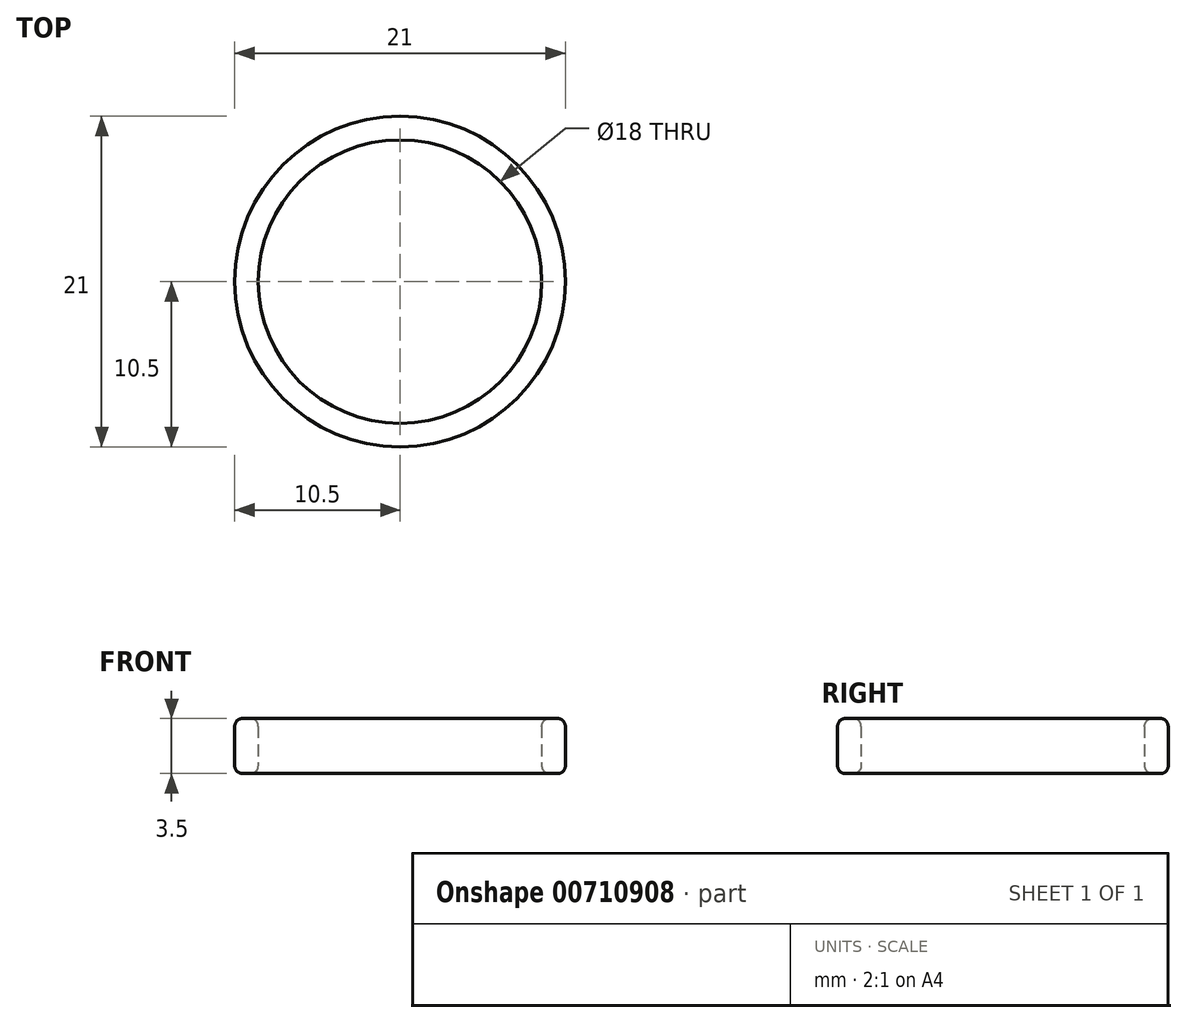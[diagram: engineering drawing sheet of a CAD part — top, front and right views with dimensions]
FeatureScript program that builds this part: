
annotation { "Feature Type Name" : "Feature", "Feature Type Description" : "" }
export const myFeature = defineFeature(function(context is Context, id is Id, definition is map)
    precondition{}
    {
        {
            var Q0;
            Q0=qCreatedBy(makeId("Front.planeOp"),FACE);
            var sketch = newSketch(context, id + "F0", { "sketchPlane" : qUnion([Q0])});
            skLineSegment(sketch, "E0.bottom", {"start": v(9, 4.67) * mm, "end": v(10.5, 4.67) * mm});
            skLineSegment(sketch, "E0.top", {"start": v(9, 8.17) * mm, "end": v(10.5, 8.17) * mm});
            skLineSegment(sketch, "E0.left", {"start": v(9, 4.67) * mm, "end": v(9, 8.17) * mm});
            skLineSegment(sketch, "E0.right", {"start": v(10.5, 4.67) * mm, "end": v(10.5, 8.17) * mm});
            skLineSegment(sketch, "E1", {"start": v(0, 0.46) * mm, "end": v(0, 3.72) * mm});
            skSolve(sketch);
        }
        {
            var Q0;
            Q0 = qSketchRegion(id + "F0", true);
            var Q1;
            Q1=sQuery(id+"F0.wireOp",EDGE,"E1");
            revolve(context, id + "F1", {"surfaceOperationType" : NewSurfaceOperationType.NEW, "entities" : qUnion([Q0]), "axis" : qUnion([Q1]), "revolveType" : RevolveType.FULL});
        }
        {
            var Q0;
            Q0=makeQuery(id+"F1.opRevolve","SWEPT_EDGE",EDGE,{"disambiguationData":[OSD([sQuery(id+"F0.wireOp",EDGE,"E0.top"),sQuery(id+"F0.wireOp",EDGE,"E0.right")])]});
            var Q1;
            Q1=makeQuery(id+"F1.opRevolve","SWEPT_EDGE",EDGE,{"disambiguationData":[OSD([sQuery(id+"F0.wireOp",EDGE,"E0.top"),sQuery(id+"F0.wireOp",EDGE,"E0.left")])]});
            var Q2;
            Q2=makeQuery(id+"F1.opRevolve","SWEPT_EDGE",EDGE,{"disambiguationData":[OSD([sQuery(id+"F0.wireOp",EDGE,"E0.bottom"),sQuery(id+"F0.wireOp",EDGE,"E0.left")])]});
            var Q3;
            Q3=makeQuery(id+"F1.opRevolve","SWEPT_EDGE",EDGE,{"disambiguationData":[OSD([sQuery(id+"F0.wireOp",EDGE,"E0.bottom"),sQuery(id+"F0.wireOp",EDGE,"E0.right")])]});
            fillet(context, id + "F2", {"entities" : qUnion([Q0, Q1, Q2, Q3]), "radius" : 0.5 * mm, "tangentPropagation" : true, "allowEdgeOverflow" : false});
        }
    });
